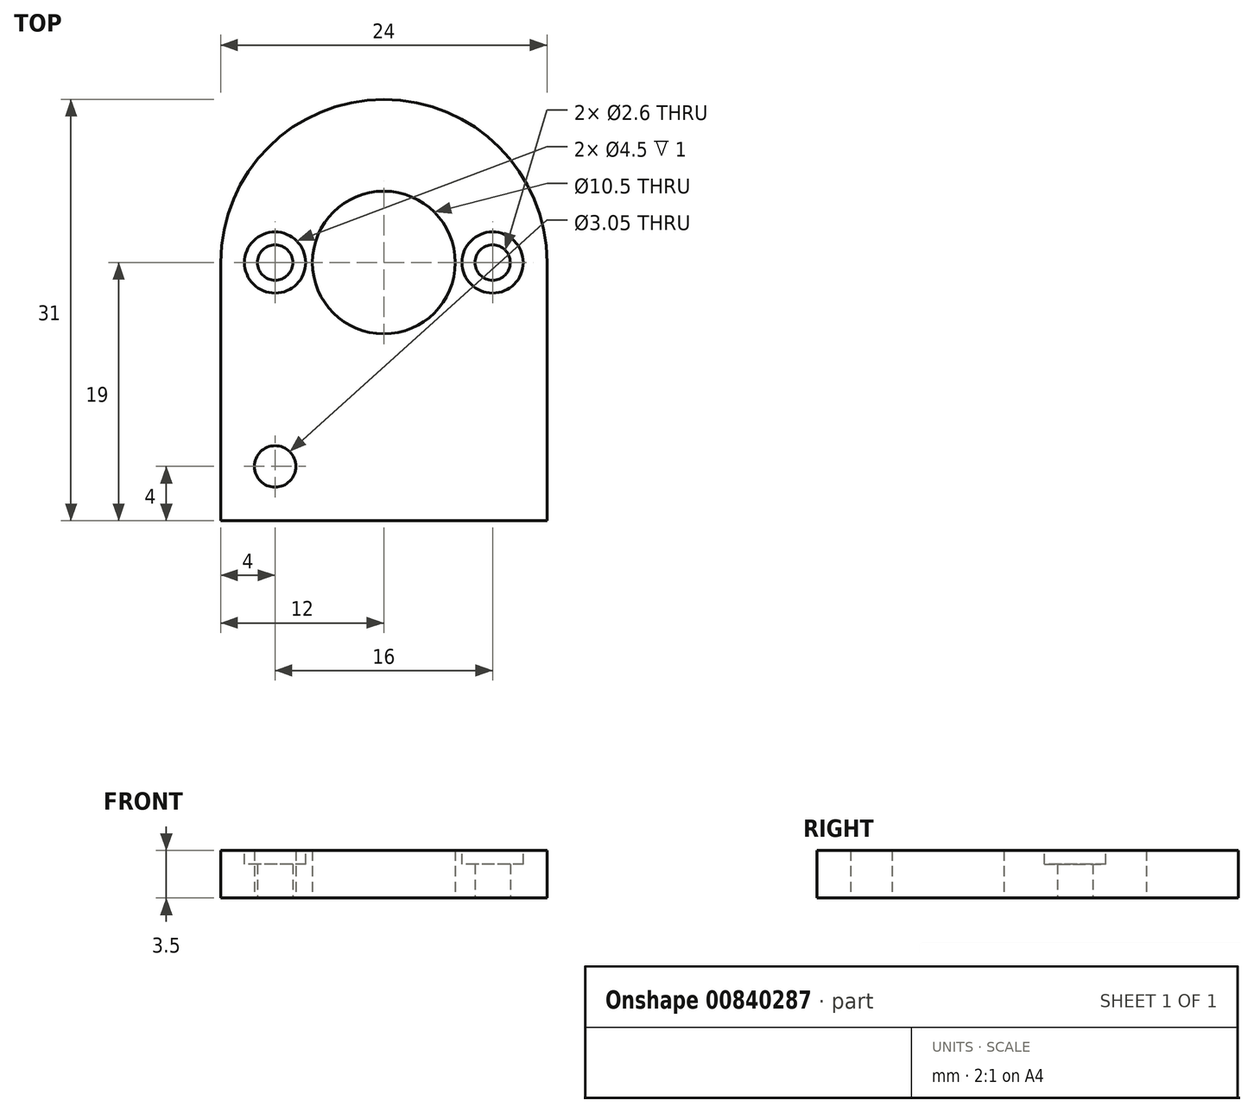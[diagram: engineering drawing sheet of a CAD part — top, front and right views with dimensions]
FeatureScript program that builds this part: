
annotation { "Feature Type Name" : "Feature", "Feature Type Description" : "" }
export const myFeature = defineFeature(function(context is Context, id is Id, definition is map)
    precondition{}
    {
        {
            var Q0;
            Q0=qCreatedBy(makeId("Top.planeOp"),FACE);
            var sketch = newSketch(context, id + "F0", { "sketchPlane" : qUnion([Q0])});
            skLineSegment(sketch, "E0", {"start": v(-12, -9.5) * mm, "end": v(12, -9.5) * mm});
            skLineSegment(sketch, "E1", {"start": v(12, -9.5) * mm, "end": v(12, 9.5) * mm});
            skLineSegment(sketch, "E2", {"start": v(-12, -9.5) * mm, "end": v(-12, 9.5) * mm});
            skLineSegment(sketch, "E3", {"start": v(-12, 9.5) * mm, "end": v(12, 9.5) * mm, "construction": true});
            skArc(sketch, "E4", {"start": v(-12, 9.5) * mm, "mid": v(0, 21.5) * mm, "end": v(12, 9.5) * mm});
            skCircle(sketch, "E5", {"center": v(0, 9.5) * mm, "radius": 5.25 * mm});
            skCircle(sketch, "E6", {"center": v(-8, 9.5) * mm, "radius": 1.3 * mm});
            skCircle(sketch, "E7", {"center": v(8, 9.5) * mm, "radius": 1.3 * mm});
            skLineSegment(sketch, "E8", {"start": v(-8, 9.5) * mm, "end": v(-8, -5.5) * mm, "construction": true});
            skCircle(sketch, "E9", {"center": v(-8, -5.5) * mm, "radius": 1.52 * mm});
            skSolve(sketch);
        }
        {
            var Q0;
            Q0 = qSketchRegion(id + "F0", true);
            extrude(context, id + "F1", {"entities" : qUnion([Q0]), "depth" : 3.5 * mm, "offsetDistance" : 25 * mm});
        }
        {
            var Q0;
            Q0=makeQuery(id+"F1.opExtrude","CAP_FACE",FACE,{"disambiguationData":[OSD([sQuery(id+"F0.wireOp",EDGE,"E0"),sQuery(id+"F0.wireOp",EDGE,"E1"),sQuery(id+"F0.wireOp",EDGE,"E2"),sQuery(id+"F0.wireOp",EDGE,"E4"),sQuery(id+"F0.wireOp",EDGE,"E5"),sQuery(id+"F0.wireOp",EDGE,"E6"),sQuery(id+"F0.wireOp",EDGE,"E7"),sQuery(id+"F0.wireOp",EDGE,"E9")])],"isStart":false});
            var sketch = newSketch(context, id + "F2", { "sketchPlane" : qUnion([Q0])});
            skCircle(sketch, "E10", {"center": v(-8, 9.5) * mm, "radius": 2.25 * mm});
            skCircle(sketch, "E11", {"center": v(8, 9.5) * mm, "radius": 2.25 * mm});
            skSolve(sketch);
        }
        {
            var Q0;
            Q0 = qSketchRegion(id + "F2", true);
            extrude(context, id + "F3", {"entities" : qUnion([Q0]), "operationType" : NewBodyOperationType.REMOVE, "oppositeDirection" : true, "depth" : 1 * mm, "offsetDistance" : 25 * mm});
        }
    });
